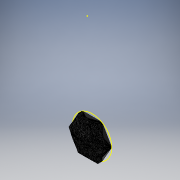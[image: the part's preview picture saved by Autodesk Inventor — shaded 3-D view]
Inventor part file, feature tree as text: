
AUTODESK INVENTOR PART (.ipt)
format: ipt  version: 2018 (Build 220112000, 112)  size: 248,320 bytes
history: native  units: in
note: dims shown in document units (in); Inventor stores cm internally (conversion verified against a paired STEP export)
features: other x2, sketch x1
ambient origin geometry x8: Origin, YZ Plane, XZ Plane, XY Plane, X Axis, Y Axis, Z Axis, Center Point
feature tree (3):
  other  "TMOceanTile1Final2019"
  sketch  "Sketch1"
  other  "MeshFeature1"
